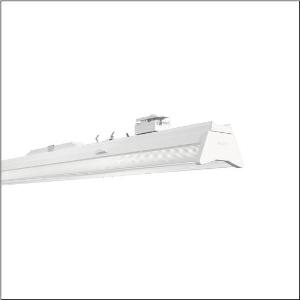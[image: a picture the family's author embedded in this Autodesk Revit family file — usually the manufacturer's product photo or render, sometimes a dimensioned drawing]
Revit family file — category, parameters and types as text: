
# Revit family: licross_r__11_performance_mo_51tm16cn49xg_d1b9
name_source: partatom
category: Lighting Fixtures
units: mm (PartAtom-declared; Revit-internal decimal feet)

## family parameters
Cut with Voids When Loaded = No
Host = Face
Light Source = No
Part Type = Normal
Room Calculation Point = No
Round Connector Dimension = Use Diameter
Shared = No

## types (1)
- --- (1 x LED, 9190 lm, 49.4 W, 4000K)
    Apparent Load = 49 VA
    CIE Flux Codes = 66 88 96 79 100
    Color Rendering = 80
    Color Temperature = 4000K
    Default Elevation = 1800 mm
    Description = Licross® 11 Performance MO, luminaire insert, of sheet steel, galvanised, coil coated, white, length: 1.500mm, width: 120mm, height: 123mm, LED rated luminous flux: 9.190lm, light colour: 840, control gear: ON/OFF Multilumen, CLOi, with plug, 3-pole, with phase selection, mains connection: 220..240V, AC, 50/60Hz, start of lifetime: 49W, end of service life: 55W, halogen-free wiring, primary light control with lens, of plastic, primary optical cover: cover, of PMMA, light emission: direct/indirect distribution, primary light characteristic: symmetric, protection rating (complete): IP40, insulation class (complete): insulation class I (protective earthing), certification: CE, ENEC, VDE, UKCA, protection symbol: D if used in an environment without relevant dust loads with corresponding accessories, impact resistance: IK06, permissible ambient temperature for indoor applications: -35..+40°C, corresponds to IFS (International Featured Standards) requirements for safety and quality in the food industry, reducing of maximum allowable ambient temperature of 5°C with ceiling mounting, LABS conformity tested according to VDMA 24364:2018-05, packaging unit: 1 piece
    Height = 114 mm
    Lamp = 1 x LED
    Lamp Light Flux = 9190 lm
    Lamp Power = 49.4 W
    Lamp count = 1
    Length = 1500 mm
    Luminous efficacy = 186 lm/W
    Manufacturer = Siteco
    ModVariant = No
    Model = 51TM16CN49XG
    Mounting Place = Ceiling
    Mounting Type = Pendant
    Number of Poles = 1
    OnlyDefault = Yes
    Power Factor = 1
    Product Name = Licross® 11 Performance MO
    Product group = luminaire insert
    ProductGroupID = 901
    Protection Class = Protection class I
    Protection Degree = IP 40
    RLX_Detail_Level = 1
    RLX_Emergency_Light_Flux = 0 lm
    RLX_Emergency_Type = 0
    RLX_Emergency_Type_DB = No
    RlxData = <blob elided: 31889 chars, md5=f8a7e58e>
    Socket = socket
    Standby Power = 0 W
    System Light Flux = 9190 lm
    System Power = 49 W
    Type Comments = factory setting: luminous flux: 100 % | (A | C | E) | 113 mA
    Type Image = l_1256138.jpg
    URL = http://relux.com
    VarID = @adj_055449
    Voltage = 0 V
    Weight = 0.00 kg
    Width = 120 mm

## geometry (parser evidence)
native form markers: Blend x4, Sweep x11
no freeform markers — native parametric forms only
